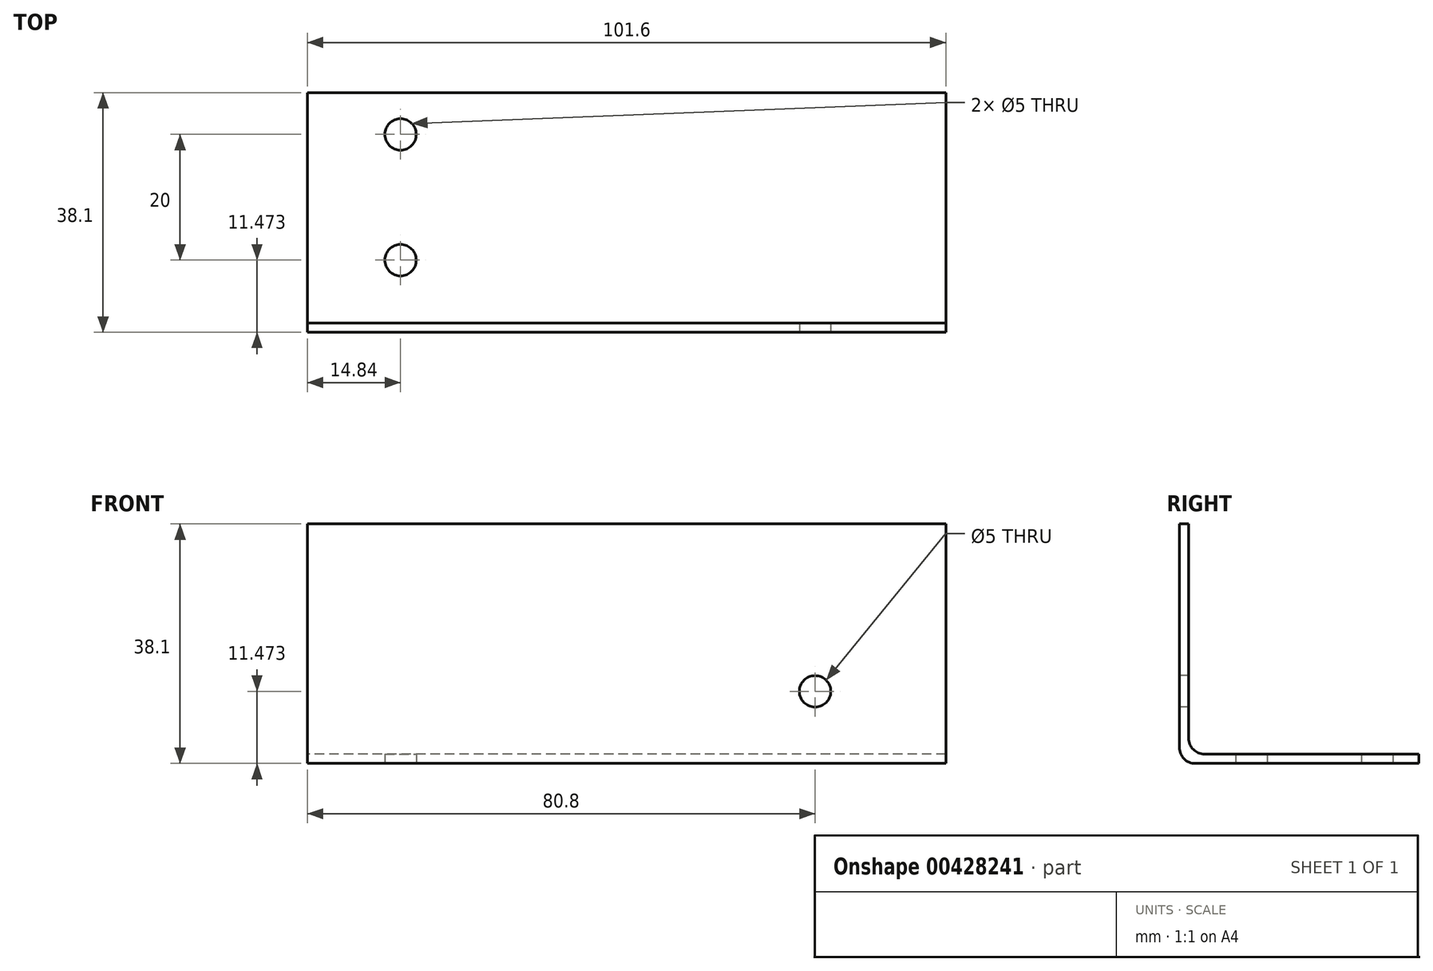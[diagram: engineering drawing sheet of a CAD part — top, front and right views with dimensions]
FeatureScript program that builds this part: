
annotation { "Feature Type Name" : "Feature", "Feature Type Description" : "" }
export const myFeature = defineFeature(function(context is Context, id is Id, definition is map)
    precondition{}
    {
        {
            var Q0;
            Q0=qCreatedBy(makeId("Right.planeOp"),FACE);
            var sketch = newSketch(context, id + "F0", { "sketchPlane" : qUnion([Q0])});
            skLineSegment(sketch, "E0.bottom", {"start": v(0, 0) * mm, "end": v(0, 0) * mm});
            skLineSegment(sketch, "E1", {"start": v(0, 0) * mm, "end": v(38.1, 0) * mm, "construction": true});
            skLineSegment(sketch, "E2", {"start": v(38.1, 0) * mm, "end": v(38.1, 1.47) * mm, "construction": true});
            skLineSegment(sketch, "E3", {"start": v(38.1, 1.47) * mm, "end": v(1.47, 1.47) * mm, "construction": true});
            skLineSegment(sketch, "E4", {"start": v(1.47, 1.47) * mm, "end": v(1.47, 38.1) * mm, "construction": true});
            skLineSegment(sketch, "E5", {"start": v(1.47, 38.1) * mm, "end": v(0, 38.1) * mm, "construction": true});
            skLineSegment(sketch, "E6", {"start": v(0, 38.1) * mm, "end": v(0, 0) * mm, "construction": true});
            skLineSegment(sketch, "E7", {"start": v(0, 38.1) * mm, "end": v(0, 2.54) * mm});
            skLineSegment(sketch, "E8", {"start": v(2.54, 0) * mm, "end": v(38.1, 0) * mm});
            skLineSegment(sketch, "E9", {"start": v(38.1, 0) * mm, "end": v(38.1, 1.47) * mm});
            skLineSegment(sketch, "E10", {"start": v(38.1, 1.47) * mm, "end": v(4.01, 1.47) * mm});
            skLineSegment(sketch, "E11", {"start": v(1.47, 4.01) * mm, "end": v(1.47, 38.1) * mm});
            skLineSegment(sketch, "E12", {"start": v(1.47, 38.1) * mm, "end": v(0, 38.1) * mm});
            skPoint(sketch, "E13.visualSharp", {"position": v(1.47, 1.47) * mm});
            skArc(sketch, "E13.filletArc", {"start": v(1.47, 4.01) * mm, "mid": v(2.22, 2.22) * mm, "end": v(4.01, 1.47) * mm});
            skPoint(sketch, "E14.visualSharp", {"position": v(0, 0) * mm});
            skArc(sketch, "E14.filletArc", {"start": v(0, 2.54) * mm, "mid": v(0.74, 0.74) * mm, "end": v(2.54, 0) * mm});
            skSolve(sketch);
        }
        {
            var Q0;
            Q0=makeQuery(id+"F0.imprint","IMPRINT",FACE,{"disambiguationData":[TD([[makeQuery(id+"F0.imprint","IMPRINT",EDGE,{"derivedFrom":sQuery(id+"F0.wireOp",EDGE,"E7")}),1.0]])]});
            extrude(context, id + "F1", {"entities" : qUnion([Q0]), "depth" : 101.6 * mm, "symmetric" : true});
        }
        {
            var Q0;
            Q0=qCreatedBy(makeId("Top.planeOp"),FACE);
            var sketch = newSketch(context, id + "F2", { "sketchPlane" : qUnion([Q0])});
            skLineSegment(sketch, "E15", {"start": v(-50.07, 11.47) * mm, "end": v(52.33, 11.47) * mm, "construction": true});
            skLineSegment(sketch, "E16", {"start": v(-52.08, 31.47) * mm, "end": v(54.69, 31.47) * mm, "construction": true});
            skCircle(sketch, "E17", {"center": v(-35.96, 11.47) * mm, "radius": 2.5 * mm});
            skCircle(sketch, "E18", {"center": v(-35.96, 31.47) * mm, "radius": 2.5 * mm});
            skLineSegment(sketch, "E19", {"start": v(0, 0) * mm, "end": v(0, 46.38) * mm, "construction": true});
            skCircle(sketch, "E20.MirrorC", {"center": v(35.96, 11.47) * mm, "radius": 2.5 * mm});
            skCircle(sketch, "E21.MirrorC", {"center": v(35.96, 31.47) * mm, "radius": 2.5 * mm});
            skSolve(sketch);
        }
        {
            var Q0;
            Q0=makeQuery(id+"F2.imprint","IMPRINT",FACE,{"disambiguationData":[TD([[makeQuery(id+"F2.imprint","IMPRINT",EDGE,{"derivedFrom":sQuery(id+"F2.wireOp",EDGE,"E20.MirrorC")}),-1.0]])]});
            var Q1;
            Q1=makeQuery(id+"F2.imprint","IMPRINT",FACE,{"disambiguationData":[TD([[makeQuery(id+"F2.imprint","IMPRINT",EDGE,{"derivedFrom":sQuery(id+"F2.wireOp",EDGE,"E21.MirrorC")}),-1.0]])]});
            var Q2;
            Q2=makeQuery(id+"F2.imprint","IMPRINT",FACE,{"disambiguationData":[TD([[makeQuery(id+"F2.imprint","IMPRINT",EDGE,{"derivedFrom":sQuery(id+"F2.wireOp",EDGE,"E18")}),1.0]])]});
            var Q3;
            Q3=makeQuery(id+"F2.imprint","IMPRINT",FACE,{"disambiguationData":[TD([[makeQuery(id+"F2.imprint","IMPRINT",EDGE,{"derivedFrom":sQuery(id+"F2.wireOp",EDGE,"E17")}),1.0]])]});
            var Q4;
            Q4=sQuery(id+"F2.wireOp",EDGE,"E18");
            var Q5;
            Q5=sQuery(id+"F2.wireOp",EDGE,"E21.MirrorC");
            var Q6;
            Q6=sQuery(id+"F2.wireOp",EDGE,"E20.MirrorC");
            var Q7;
            Q7=sQuery(id+"F2.wireOp",EDGE,"E17");
            extrude(context, id + "F3", {"entities" : qUnion([Q0, Q1, Q2, Q3]), "operationType" : NewBodyOperationType.REMOVE, "surfaceEntities" : qUnion([Q4, Q5, Q6, Q7]), "depth" : 25.4 * mm, "offsetDistance" : 25.4 * mm, "symmetric" : true});
        }
        {
            var Q0;
            Q0=qCreatedBy(makeId("Front.planeOp"),FACE);
            var sketch = newSketch(context, id + "F4", { "sketchPlane" : qUnion([Q0])});
            skLineSegment(sketch, "E22", {"start": v(0, 0) * mm, "end": v(0, 176.44) * mm, "construction": true});
            skLineSegment(sketch, "E23", {"start": v(233.74, 11.47) * mm, "end": v(-238.1, 11.47) * mm, "construction": true});
            skLineSegment(sketch, "E24", {"start": v(30, 44.85) * mm, "end": v(30, -13.55) * mm, "construction": true});
            skCircle(sketch, "E25", {"center": v(30, 11.47) * mm, "radius": 2.5 * mm});
            skCircle(sketch, "E26.MirrorC", {"center": v(-30, 11.47) * mm, "radius": 2.5 * mm});
            skSolve(sketch);
        }
        {
            var Q0;
            Q0=makeQuery(id+"F4.imprint","IMPRINT",FACE,{"disambiguationData":[TD([[makeQuery(id+"F4.imprint","IMPRINT",EDGE,{"derivedFrom":sQuery(id+"F4.wireOp",EDGE,"E26.MirrorC")}),-1.0]])]});
            var Q1;
            Q1=makeQuery(id+"F4.imprint","IMPRINT",FACE,{"disambiguationData":[TD([[makeQuery(id+"F4.imprint","IMPRINT",EDGE,{"derivedFrom":sQuery(id+"F4.wireOp",EDGE,"E25")}),1.0]])]});
            var Q2;
            Q2=sQuery(id+"F4.wireOp",EDGE,"E25");
            extrude(context, id + "F5", {"entities" : qUnion([Q0, Q1]), "operationType" : NewBodyOperationType.REMOVE, "surfaceEntities" : qUnion([Q2]), "oppositeDirection" : true, "depth" : 25.4 * mm, "offsetDistance" : 25.4 * mm, "symmetric" : true});
        }
    });
